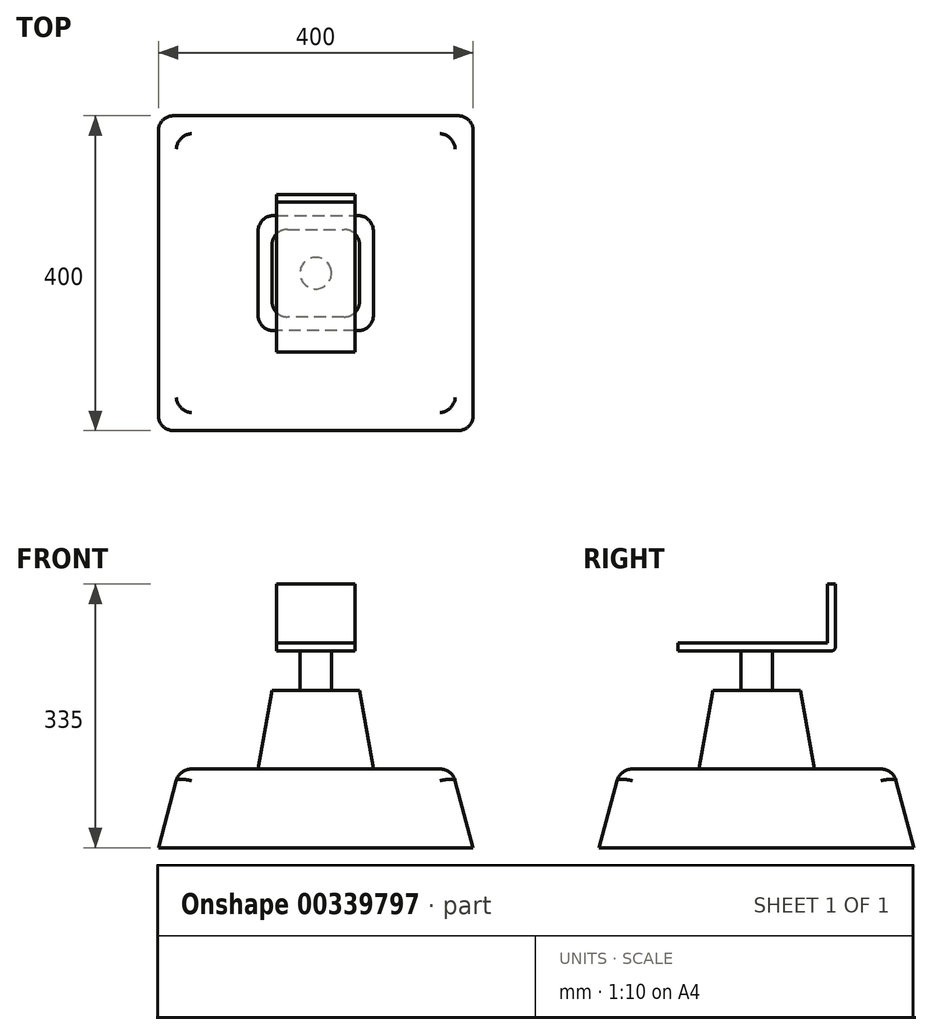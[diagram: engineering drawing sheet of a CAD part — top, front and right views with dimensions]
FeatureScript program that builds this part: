
annotation { "Feature Type Name" : "Feature", "Feature Type Description" : "" }
export const myFeature = defineFeature(function(context is Context, id is Id, definition is map)
    precondition{}
    {
        {
            var Q0;
            Q0=qCreatedBy(makeId("Top.planeOp"),FACE);
            var sketch = newSketch(context, id + "F0", { "sketchPlane" : qUnion([Q0])});
            skLineSegment(sketch, "E0.bottom", {"start": v(0, 0) * mm, "end": v(400, 0) * mm});
            skLineSegment(sketch, "E0.top", {"start": v(0, 400) * mm, "end": v(400, 400) * mm});
            skLineSegment(sketch, "E0.left", {"start": v(0, 0) * mm, "end": v(0, 400) * mm});
            skLineSegment(sketch, "E0.right", {"start": v(400, 0) * mm, "end": v(400, 400) * mm});
            skSolve(sketch);
        }
        {
            var Q0;
            Q0 = qSketchRegion(id + "F0", true);
            extrude(context, id + "F1", {"entities" : qUnion([Q0]), "depth" : 100 * mm, "hasDraft" : true, "draftAngle" : 15 * degree, "draftPullDirection" : true});
        }
        {
            var Q0;
            Q0=makeQuery(id+"F1.opExtrude","CAP_FACE",FACE,{"disambiguationData":[OSD([sQuery(id+"F0.wireOp",EDGE,"E0.bottom"),sQuery(id+"F0.wireOp",EDGE,"E0.top"),sQuery(id+"F0.wireOp",EDGE,"E0.left"),sQuery(id+"F0.wireOp",EDGE,"E0.right")])],"isStart":false});
            var sketch = newSketch(context, id + "F2", { "sketchPlane" : qUnion([Q0])});
            skLineSegment(sketch, "E1.0", {"start": v(126.8, 273.2) * mm, "end": v(273.2, 273.2) * mm});
            skLineSegment(sketch, "E1.1", {"start": v(126.8, 126.8) * mm, "end": v(126.8, 273.2) * mm});
            skLineSegment(sketch, "E1.2", {"start": v(126.8, 126.8) * mm, "end": v(273.2, 126.8) * mm});
            skLineSegment(sketch, "E1.3", {"start": v(273.2, 126.8) * mm, "end": v(273.2, 273.2) * mm});
            skSolve(sketch);
        }
        {
            var Q0;
            Q0=makeQuery(id+"F2.imprint","IMPRINT",FACE,{"disambiguationData":[TD([[makeQuery(id+"F2.imprint","IMPRINT",EDGE,{"derivedFrom":sQuery(id+"F2.wireOp",EDGE,"E1.0")}),-1.0]])]});
            extrude(context, id + "F3", {"entities" : qUnion([Q0]), "operationType" : NewBodyOperationType.ADD, "depth" : 100 * mm, "hasDraft" : true, "draftAngle" : 10 * degree, "draftPullDirection" : true});
        }
        {
            var Q0;
            Q0=makeQuery(id+"F1.opExtrude","SWEPT_EDGE",EDGE,{"disambiguationData":[OSD([sQuery(id+"F0.wireOp",EDGE,"E0.bottom"),sQuery(id+"F0.wireOp",EDGE,"E0.left")])]});
            var Q1;
            Q1=makeQuery(id+"F1.opExtrude","SWEPT_EDGE",EDGE,{"disambiguationData":[OSD([sQuery(id+"F0.wireOp",EDGE,"E0.bottom"),sQuery(id+"F0.wireOp",EDGE,"E0.right")])]});
            var Q2;
            Q2=makeQuery(id+"F1.opExtrude","SWEPT_EDGE",EDGE,{"disambiguationData":[OSD([sQuery(id+"F0.wireOp",EDGE,"E0.top"),sQuery(id+"F0.wireOp",EDGE,"E0.left")])]});
            var Q3;
            Q3=makeQuery(id+"F1.opExtrude","SWEPT_EDGE",EDGE,{"disambiguationData":[OSD([sQuery(id+"F0.wireOp",EDGE,"E0.top"),sQuery(id+"F0.wireOp",EDGE,"E0.right")])]});
            var Q4;
            Q4=makeQuery(id+"F1.opExtrude","CAP_EDGE",EDGE,{"disambiguationData":[OSD([sQuery(id+"F0.wireOp",EDGE,"E0.top")])],"isStart":false});
            var Q5;
            Q5=makeQuery(id+"F1.opExtrude","CAP_EDGE",EDGE,{"disambiguationData":[OSD([sQuery(id+"F0.wireOp",EDGE,"E0.left")])],"isStart":false});
            var Q6;
            Q6=makeQuery(id+"F1.opExtrude","CAP_EDGE",EDGE,{"disambiguationData":[OSD([sQuery(id+"F0.wireOp",EDGE,"E0.bottom")])],"isStart":false});
            var Q7;
            Q7=makeQuery(id+"F1.opExtrude","CAP_EDGE",EDGE,{"disambiguationData":[OSD([sQuery(id+"F0.wireOp",EDGE,"E0.right")])],"isStart":false});
            var Q8;
            Q8=makeQuery(id+"F3.opExtrude","CAP_EDGE",EDGE,{"disambiguationData":[OSD([sQuery(id+"F2.wireOp",EDGE,"E1.3")])],"isStart":true});
            var Q9;
            Q9=makeQuery(id+"F3.opExtrude","CAP_EDGE",EDGE,{"disambiguationData":[OSD([sQuery(id+"F2.wireOp",EDGE,"E1.2")])],"isStart":true});
            var Q10;
            Q10=makeQuery(id+"F3.opExtrude","SWEPT_EDGE",EDGE,{"disambiguationData":[OSD([sQuery(id+"F2.wireOp",EDGE,"E1.2"),sQuery(id+"F2.wireOp",EDGE,"E1.3")])]});
            var Q11;
            Q11=makeQuery(id+"F3.opExtrude","CAP_EDGE",EDGE,{"disambiguationData":[OSD([sQuery(id+"F2.wireOp",EDGE,"E1.1")])],"isStart":true});
            var Q12;
            Q12=makeQuery(id+"F3.opExtrude","SWEPT_EDGE",EDGE,{"disambiguationData":[OSD([sQuery(id+"F2.wireOp",EDGE,"E1.1"),sQuery(id+"F2.wireOp",EDGE,"E1.2")])]});
            var Q13;
            Q13=makeQuery(id+"F3.opExtrude","CAP_EDGE",EDGE,{"disambiguationData":[OSD([sQuery(id+"F2.wireOp",EDGE,"E1.0")])],"isStart":true});
            var Q14;
            Q14=makeQuery(id+"F3.opExtrude","SWEPT_EDGE",EDGE,{"disambiguationData":[OSD([sQuery(id+"F2.wireOp",EDGE,"E1.0"),sQuery(id+"F2.wireOp",EDGE,"E1.3")])]});
            var Q15;
            Q15=makeQuery(id+"F3.opExtrude","SWEPT_EDGE",EDGE,{"disambiguationData":[OSD([sQuery(id+"F2.wireOp",EDGE,"E1.0"),sQuery(id+"F2.wireOp",EDGE,"E1.1")])]});
            fillet(context, id + "F4", {"entities" : qUnion([Q0, Q1, Q2, Q3, Q4, Q5, Q6, Q7, Q8, Q9, Q10, Q11, Q12, Q13, Q14, Q15]), "radius" : 20 * mm, "tangentPropagation" : true, "allowEdgeOverflow" : false});
        }
        {
            var Q0;
            Q0=makeQuery(id+"F3.opExtrude","CAP_FACE",FACE,{"disambiguationData":[OSD([sQuery(id+"F2.wireOp",EDGE,"E1.0"),sQuery(id+"F2.wireOp",EDGE,"E1.1"),sQuery(id+"F2.wireOp",EDGE,"E1.2"),sQuery(id+"F2.wireOp",EDGE,"E1.3")])],"isStart":false});
            var sketch = newSketch(context, id + "F5", { "sketchPlane" : qUnion([Q0])});
            skCircle(sketch, "E2", {"center": v(200, 200) * mm, "radius": 20 * mm});
            skPoint(sketch, "E2.centerSnap0", {"position": v(144.43, 200) * mm});
            skPoint(sketch, "E2.centerSnap1", {"position": v(200, 255.57) * mm});
            skSolve(sketch);
        }
        {
            var Q0;
            Q0=makeQuery(id+"F5.imprint","IMPRINT",FACE,{"disambiguationData":[TD([[makeQuery(id+"F5.imprint","IMPRINT",EDGE,{"derivedFrom":sQuery(id+"F5.wireOp",EDGE,"E2")}),1.0]])]});
            extrude(context, id + "F6", {"entities" : qUnion([Q0]), "operationType" : NewBodyOperationType.ADD, "depth" : 50 * mm});
        }
        {
            var Q0;
            Q0=makeQuery(id+"F6.opExtrude","CAP_FACE",FACE,{"disambiguationData":[OSD([sQuery(id+"F5.wireOp",EDGE,"E2")])],"isStart":false});
            var sketch = newSketch(context, id + "F7", { "sketchPlane" : qUnion([Q0])});
            skLineSegment(sketch, "E3.bottom", {"start": v(250, 300) * mm, "end": v(150, 300) * mm});
            skLineSegment(sketch, "E3.top", {"start": v(250, 100) * mm, "end": v(150, 100) * mm});
            skLineSegment(sketch, "E3.left", {"start": v(250, 300) * mm, "end": v(250, 100) * mm});
            skLineSegment(sketch, "E3.right", {"start": v(150, 300) * mm, "end": v(150, 100) * mm});
            skPoint(sketch, "E3.middle", {"position": v(200, 200) * mm});
            skSolve(sketch);
        }
        {
            var Q0;
            Q0=makeQuery(id+"F7.imprint","IMPRINT",FACE,{"disambiguationData":[TD([[makeQuery(id+"F7.imprint","IMPRINT",EDGE,{"derivedFrom":sQuery(id+"F7.wireOp",EDGE,"E3.bottom")}),1.0]])]});
            var Q1;
            Q1=makeQuery(id+"F7.imprint","IMPRINT",FACE,{"disambiguationData":[TD([[makeQuery(id+"F7.imprint","IMPRINT",EDGE,{"derivedFrom":makeQuery(id+"F6.opExtrude","CAP_EDGE",EDGE,{"disambiguationData":[OSD([sQuery(id+"F5.wireOp",EDGE,"E2")])],"isStart":false})}),1.0]])]});
            extrude(context, id + "F8", {"entities" : qUnion([Q0, Q1]), "operationType" : NewBodyOperationType.ADD, "depth" : 10 * mm});
        }
        {
            var Q0;
            Q0=makeQuery(id+"F8.opExtrude","CAP_FACE",FACE,{"disambiguationData":[OSD([sQuery(id+"F7.wireOp",EDGE,"E3.bottom"),sQuery(id+"F7.wireOp",EDGE,"E3.top"),sQuery(id+"F7.wireOp",EDGE,"E3.left"),sQuery(id+"F7.wireOp",EDGE,"E3.right")])],"isStart":false});
            var sketch = newSketch(context, id + "F9", { "sketchPlane" : qUnion([Q0])});
            skLineSegment(sketch, "E4.bottom", {"start": v(150, 300) * mm, "end": v(250, 300) * mm});
            skLineSegment(sketch, "E4.top", {"start": v(150, 290) * mm, "end": v(250, 290) * mm});
            skLineSegment(sketch, "E4.left", {"start": v(150, 300) * mm, "end": v(150, 290) * mm});
            skLineSegment(sketch, "E4.right", {"start": v(250, 300) * mm, "end": v(250, 290) * mm});
            skSolve(sketch);
        }
        {
            var Q0;
            Q0=makeQuery(id+"F9.imprint","IMPRINT",FACE,{"disambiguationData":[TD([[makeQuery(id+"F9.imprint","IMPRINT",EDGE,{"derivedFrom":sQuery(id+"F9.wireOp",EDGE,"E4.bottom")}),1.0]])]});
            extrude(context, id + "F10", {"entities" : qUnion([Q0]), "operationType" : NewBodyOperationType.ADD, "depth" : 75 * mm});
        }
        {
            var Q0;
            Q0=makeQuery(id+"F10.opExtrude","CAP_EDGE",EDGE,{"disambiguationData":[OSD([sQuery(id+"F9.wireOp",EDGE,"E4.top")])],"isStart":true});
            var Q1;
            Q1=makeQuery(id+"F8.opExtrude","CAP_EDGE",EDGE,{"disambiguationData":[OSD([sQuery(id+"F7.wireOp",EDGE,"E3.bottom")])],"isStart":true});
            fillet(context, id + "F11", {"entities" : qUnion([Q0, Q1]), "radius" : 5 * mm, "tangentPropagation" : true, "allowEdgeOverflow" : false});
        }
    });
